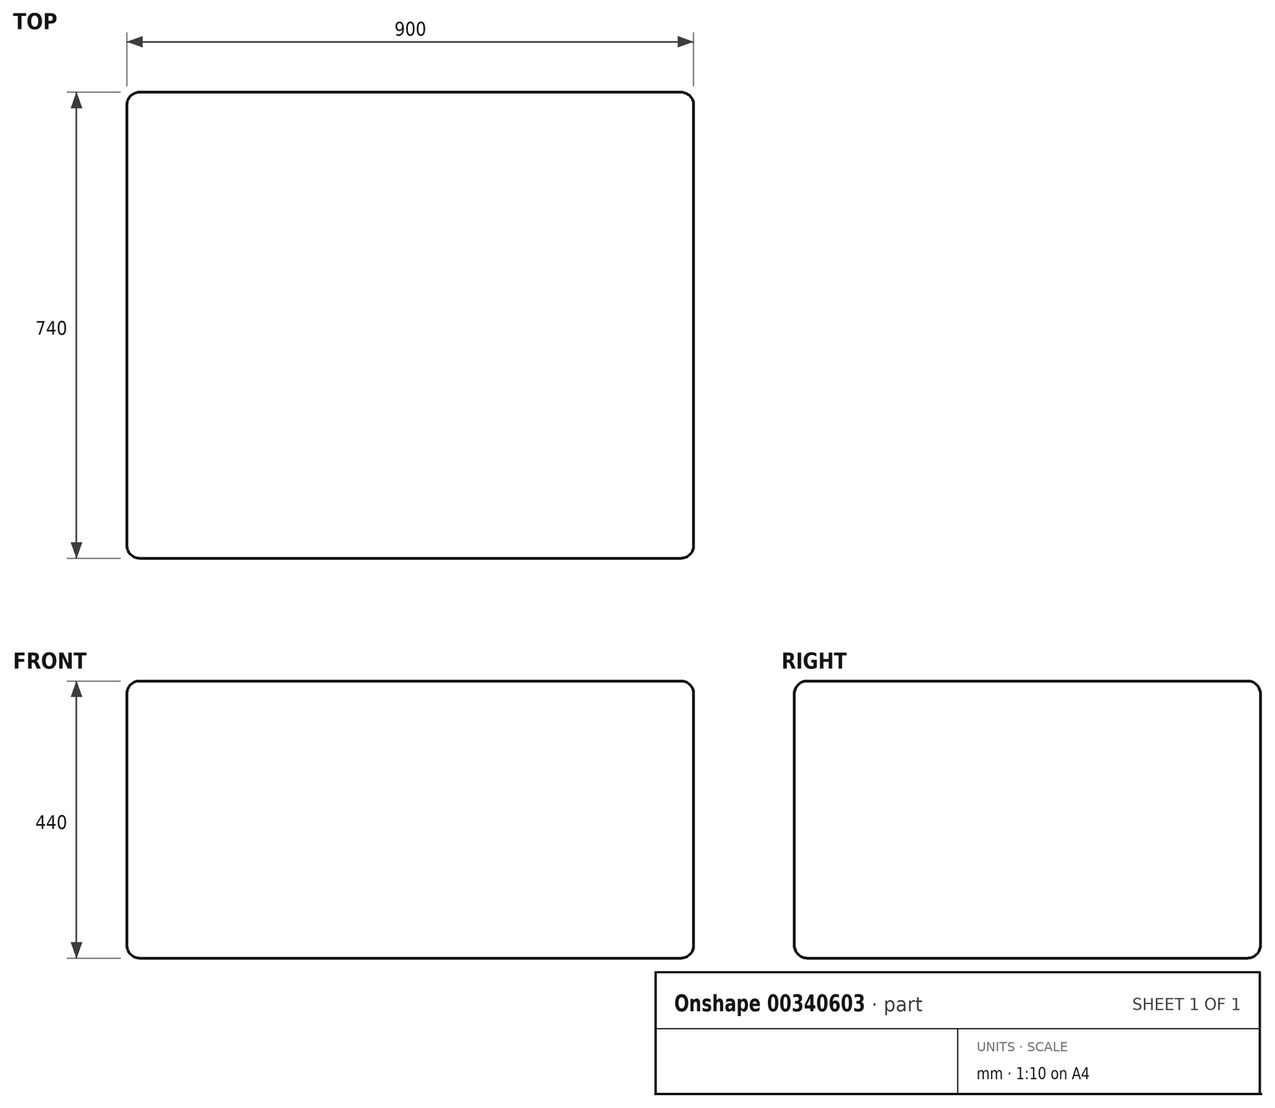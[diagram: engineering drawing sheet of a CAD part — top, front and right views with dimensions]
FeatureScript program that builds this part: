
annotation { "Feature Type Name" : "Feature", "Feature Type Description" : "" }
export const myFeature = defineFeature(function(context is Context, id is Id, definition is map)
    precondition{}
    {
        {
            var Q0;
            Q0=qCreatedBy(makeId("Top.planeOp"),FACE);
            var sketch = newSketch(context, id + "F0", { "sketchPlane" : qUnion([Q0])});
            skLineSegment(sketch, "E0.bottom", {"start": v(-795.28, 74.82) * mm, "end": v(104.72, 74.82) * mm});
            skLineSegment(sketch, "E0.top", {"start": v(-795.28, -665.18) * mm, "end": v(104.72, -665.18) * mm});
            skLineSegment(sketch, "E0.left", {"start": v(-795.28, 74.82) * mm, "end": v(-795.28, -665.18) * mm});
            skLineSegment(sketch, "E0.right", {"start": v(104.72, 74.82) * mm, "end": v(104.72, -665.18) * mm});
            skSolve(sketch);
        }
        {
            var Q0;
            Q0 = qSketchRegion(id + "F0", true);
            extrude(context, id + "F1", {"entities" : qUnion([Q0]), "depth" : 440 * mm});
        }
        {
            var Q0;
            Q0=makeQuery(id+"F1.opExtrude","SWEPT_EDGE",EDGE,{"disambiguationData":[OSD([sQuery(id+"F0.wireOp",EDGE,"E0.top"),sQuery(id+"F0.wireOp",EDGE,"E0.right")])]});
            var Q1;
            Q1=makeQuery(id+"F1.opExtrude","CAP_FACE",FACE,{"disambiguationData":[OSD([sQuery(id+"F0.wireOp",EDGE,"E0.bottom"),sQuery(id+"F0.wireOp",EDGE,"E0.top"),sQuery(id+"F0.wireOp",EDGE,"E0.left"),sQuery(id+"F0.wireOp",EDGE,"E0.right")])],"isStart":false});
            var Q2;
            Q2=makeQuery(id+"F1.opExtrude","SWEPT_EDGE",EDGE,{"disambiguationData":[OSD([sQuery(id+"F0.wireOp",EDGE,"E0.top"),sQuery(id+"F0.wireOp",EDGE,"E0.left")])]});
            var Q3;
            Q3=makeQuery(id+"F1.opExtrude","CAP_FACE",FACE,{"disambiguationData":[OSD([sQuery(id+"F0.wireOp",EDGE,"E0.bottom"),sQuery(id+"F0.wireOp",EDGE,"E0.top"),sQuery(id+"F0.wireOp",EDGE,"E0.left"),sQuery(id+"F0.wireOp",EDGE,"E0.right")])],"isStart":true});
            var Q4;
            Q4=makeQuery(id+"F1.opExtrude","SWEPT_FACE",FACE,{"disambiguationData":[OSD([sQuery(id+"F0.wireOp",EDGE,"E0.bottom")])]});
            var Q5;
            Q5=makeQuery(id+"F1.opExtrude","SWEPT_EDGE",EDGE,{"disambiguationData":[OSD([sQuery(id+"F0.wireOp",EDGE,"E0.bottom"),sQuery(id+"F0.wireOp",EDGE,"E0.left")])]});
            var Q6;
            Q6=makeQuery(id+"F1.opExtrude","SWEPT_FACE",FACE,{"disambiguationData":[OSD([sQuery(id+"F0.wireOp",EDGE,"E0.top")])]});
            var Q7;
            Q7=makeQuery(id+"F1.opExtrude","SWEPT_FACE",FACE,{"disambiguationData":[OSD([sQuery(id+"F0.wireOp",EDGE,"E0.left")])]});
            var Q8;
            Q8=makeQuery(id+"F1.opExtrude","SWEPT_EDGE",EDGE,{"disambiguationData":[OSD([sQuery(id+"F0.wireOp",EDGE,"E0.bottom"),sQuery(id+"F0.wireOp",EDGE,"E0.right")])]});
            var Q9;
            Q9=makeQuery(id+"F1.opExtrude","CAP_EDGE",EDGE,{"disambiguationData":[OSD([sQuery(id+"F0.wireOp",EDGE,"E0.bottom")])],"isStart":true});
            var Q10;
            Q10=makeQuery(id+"F1.opExtrude","CAP_EDGE",EDGE,{"disambiguationData":[OSD([sQuery(id+"F0.wireOp",EDGE,"E0.bottom")])],"isStart":false});
            var Q11;
            Q11=makeQuery(id+"F1.opExtrude","SWEPT_FACE",FACE,{"disambiguationData":[OSD([sQuery(id+"F0.wireOp",EDGE,"E0.right")])]});
            var Q12;
            Q12=makeQuery(id+"F1.opExtrude","CAP_EDGE",EDGE,{"disambiguationData":[OSD([sQuery(id+"F0.wireOp",EDGE,"E0.top")])],"isStart":true});
            var Q13;
            Q13=makeQuery(id+"F1.opExtrude","CAP_EDGE",EDGE,{"disambiguationData":[OSD([sQuery(id+"F0.wireOp",EDGE,"E0.top")])],"isStart":false});
            var Q14;
            Q14=makeQuery(id+"F1.opExtrude","CAP_EDGE",EDGE,{"disambiguationData":[OSD([sQuery(id+"F0.wireOp",EDGE,"E0.left")])],"isStart":true});
            var Q15;
            Q15=makeQuery(id+"F1.opExtrude","CAP_EDGE",EDGE,{"disambiguationData":[OSD([sQuery(id+"F0.wireOp",EDGE,"E0.left")])],"isStart":false});
            var Q16;
            Q16=makeQuery(id+"F1.opExtrude","CAP_EDGE",EDGE,{"disambiguationData":[OSD([sQuery(id+"F0.wireOp",EDGE,"E0.right")])],"isStart":true});
            var Q17;
            Q17=makeQuery(id+"F1.opExtrude","CAP_EDGE",EDGE,{"disambiguationData":[OSD([sQuery(id+"F0.wireOp",EDGE,"E0.right")])],"isStart":false});
            fillet(context, id + "F2", {"entities" : qUnion([Q0, Q1, Q2, Q3, Q4, Q5, Q6, Q7, Q8, Q9, Q10, Q11, Q12, Q13, Q14, Q15, Q16, Q17]), "radius" : 20 * mm, "tangentPropagation" : true, "allowEdgeOverflow" : false});
        }
    });
